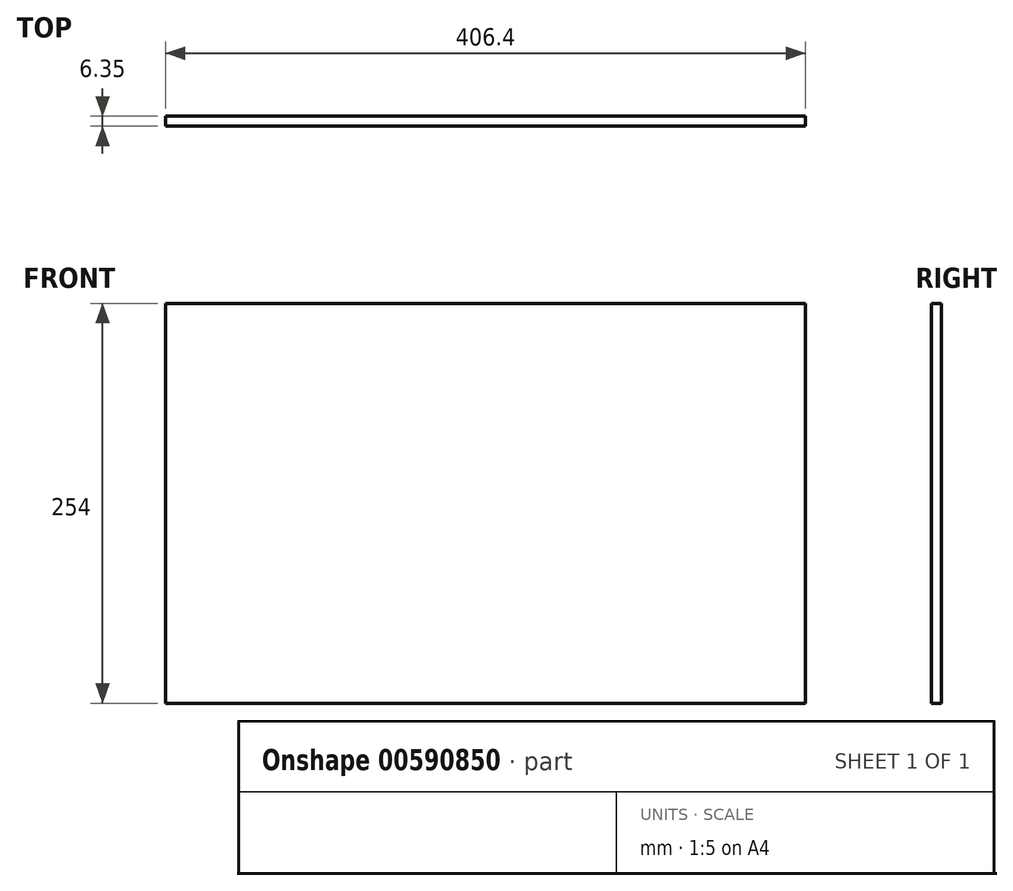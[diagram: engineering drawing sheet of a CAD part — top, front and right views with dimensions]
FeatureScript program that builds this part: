
annotation { "Feature Type Name" : "Feature", "Feature Type Description" : "" }
export const myFeature = defineFeature(function(context is Context, id is Id, definition is map)
    precondition{}
    {
        {
            var Q0;
            Q0=qCreatedBy(makeId("Front.planeOp"),FACE);
            var sketch = newSketch(context, id + "F0", { "sketchPlane" : qUnion([Q0])});
            skLineSegment(sketch, "E0.bottom", {"start": v(-184.92, 103.24) * mm, "end": v(221.48, 103.24) * mm});
            skLineSegment(sketch, "E0.top", {"start": v(-184.92, -150.76) * mm, "end": v(221.48, -150.76) * mm});
            skLineSegment(sketch, "E0.left", {"start": v(-184.92, 103.24) * mm, "end": v(-184.92, -150.76) * mm});
            skLineSegment(sketch, "E0.right", {"start": v(221.48, 103.24) * mm, "end": v(221.48, -150.76) * mm});
            skSolve(sketch);
        }
        {
            var Q0;
            Q0=makeQuery(id+"F0.imprint","IMPRINT",FACE,{"disambiguationData":[TD([[makeQuery(id+"F0.imprint","IMPRINT",EDGE,{"derivedFrom":sQuery(id+"F0.wireOp",EDGE,"E0.bottom")}),-1.0]])]});
            extrude(context, id + "F1", {"entities" : qUnion([Q0]), "depth" : 6.35 * mm, "offsetDistance" : 25.4 * mm});
        }
    });
